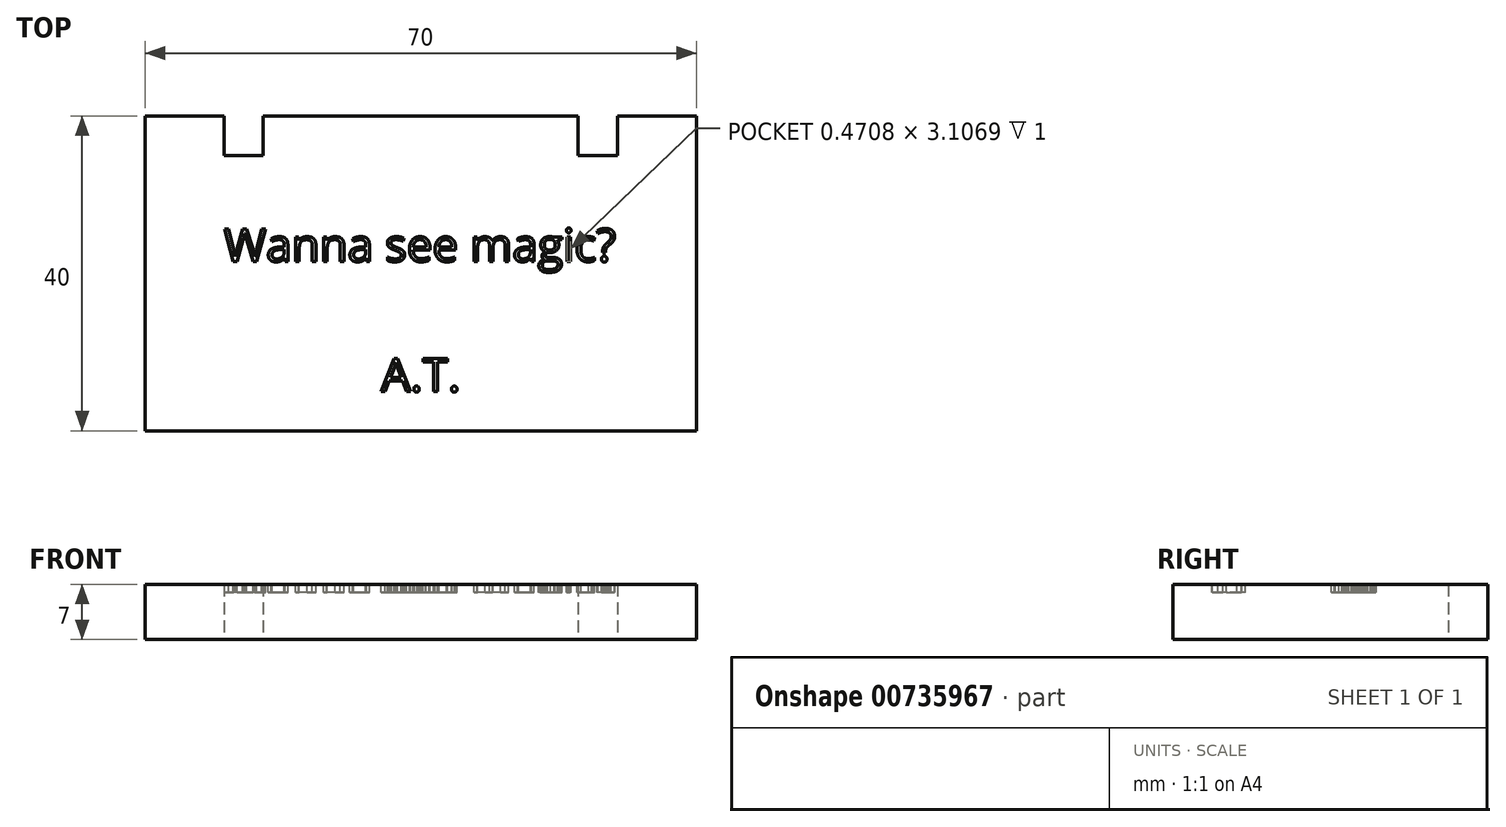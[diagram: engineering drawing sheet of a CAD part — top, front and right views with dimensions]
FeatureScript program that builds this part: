
annotation { "Feature Type Name" : "Feature", "Feature Type Description" : "" }
export const myFeature = defineFeature(function(context is Context, id is Id, definition is map)
    precondition{}
    {
        {
            var Q0;
            Q0=qCreatedBy(makeId("Top.planeOp"),FACE);
            var sketch = newSketch(context, id + "F0", { "sketchPlane" : qUnion([Q0])});
            skLineSegment(sketch, "E0.bottom", {"start": v(-31.4, 16.46) * mm, "end": v(38.6, 16.46) * mm});
            skLineSegment(sketch, "E0.top", {"start": v(-31.4, -23.54) * mm, "end": v(38.6, -23.54) * mm});
            skLineSegment(sketch, "E0.left", {"start": v(-31.4, 16.46) * mm, "end": v(-31.4, -23.54) * mm});
            skLineSegment(sketch, "E0.right", {"start": v(38.6, 16.46) * mm, "end": v(38.6, -23.54) * mm});
            skSolve(sketch);
        }
        {
            var Q0;
            Q0=makeQuery(id+"F0.imprint","IMPRINT",FACE,{"disambiguationData":[TD([[makeQuery(id+"F0.imprint","IMPRINT",EDGE,{"derivedFrom":sQuery(id+"F0.wireOp",EDGE,"E0.bottom")}),-1.0]])]});
            extrude(context, id + "F1", {"entities" : qUnion([Q0]), "depth" : 7 * mm, "offsetDistance" : 25 * mm});
        }
        {
            var Q0;
            Q0=makeQuery(id+"F1.opExtrude","SWEPT_FACE",FACE,{"disambiguationData":[OSD([sQuery(id+"F0.wireOp",EDGE,"E0.bottom")])]});
            var sketch = newSketch(context, id + "F2", { "sketchPlane" : qUnion([Q0])});
            skLineSegment(sketch, "E1.bottom", {"start": v(-28.6, 7) * mm, "end": v(-23.6, 7) * mm});
            skLineSegment(sketch, "E1.top", {"start": v(-28.6, 0) * mm, "end": v(-23.6, 0) * mm});
            skLineSegment(sketch, "E1.left", {"start": v(-28.6, 7) * mm, "end": v(-28.6, 0) * mm});
            skLineSegment(sketch, "E1.right", {"start": v(-23.6, 7) * mm, "end": v(-23.6, 0) * mm});
            skLineSegment(sketch, "E2.bottom", {"start": v(16.4, 7) * mm, "end": v(21.4, 7) * mm});
            skLineSegment(sketch, "E2.top", {"start": v(16.4, 0) * mm, "end": v(21.4, 0) * mm});
            skLineSegment(sketch, "E2.left", {"start": v(16.4, 7) * mm, "end": v(16.4, 0) * mm});
            skLineSegment(sketch, "E2.right", {"start": v(21.4, 7) * mm, "end": v(21.4, 0) * mm});
            skSolve(sketch);
        }
        {
            var Q0;
            Q0=makeQuery(id+"F2.imprint","IMPRINT",FACE,{"disambiguationData":[TD([[makeQuery(id+"F2.imprint","IMPRINT",EDGE,{"derivedFrom":sQuery(id+"F2.wireOp",EDGE,"E1.bottom")}),1.0]])]});
            var Q1;
            Q1=makeQuery(id+"F2.imprint","IMPRINT",FACE,{"disambiguationData":[TD([[makeQuery(id+"F2.imprint","IMPRINT",EDGE,{"derivedFrom":sQuery(id+"F2.wireOp",EDGE,"E2.bottom")}),1.0]])]});
            extrude(context, id + "F3", {"entities" : qUnion([Q0, Q1]), "operationType" : NewBodyOperationType.REMOVE, "oppositeDirection" : true, "depth" : 5 * mm, "offsetDistance" : 25 * mm});
        }
        {
            var Q0;
            Q0=makeQuery(id+"F1.opExtrude","CAP_FACE",FACE,{"disambiguationData":[OSD([sQuery(id+"F0.wireOp",EDGE,"E0.bottom"),sQuery(id+"F0.wireOp",EDGE,"E0.top"),sQuery(id+"F0.wireOp",EDGE,"E0.left"),sQuery(id+"F0.wireOp",EDGE,"E0.right")])],"isStart":false});
            var sketch = newSketch(context, id + "F4", { "sketchPlane" : qUnion([Q0])});
            skText(sketch, "E3", { "text": "Wanna see magic?", "fontName": "OpenSans-Regular.ttf"});
            skText(sketch, "E4", { "text": "A.T.", "fontName": "OpenSans-Regular.ttf"});
            const initialGuessF4  = {"E3": [-0.0214, -0.00202, 1, 0, 0.00418], "E4": [-0.0014, -0.01854, 1, 0, 0.00421]};
            skSetInitialGuess(sketch, initialGuessF4);
            skSolve(sketch);
        }
        {
            var Q0;
            Q0 = qSketchRegion(id + "F4", true);
            extrude(context, id + "F5", {"entities" : qUnion([Q0]), "operationType" : NewBodyOperationType.REMOVE, "oppositeDirection" : true, "depth" : 1 * mm, "offsetDistance" : 25 * mm});
        }
    });
